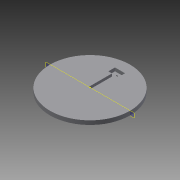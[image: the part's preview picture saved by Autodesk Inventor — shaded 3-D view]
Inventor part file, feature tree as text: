
AUTODESK INVENTOR PART (.ipt)
format: ipt  version: 2015 SP1 (Build 190203100, 203)  size: 104,960 bytes
history: native  units: mm
features: sketch x5, extrude x4, other x1, projected_geometry x1
ambient origin geometry x8: Origin, YZ Plane, XZ Plane, XY Plane, X Axis, Y Axis, Z Axis, Center Point
bodies: Body1 (feature_tree)
feature tree (11):
  other  "Sólido1"
  extrude  "Extrusión1"  Depth=6.0mm TaperAngle=0.0deg
  sketch  "Boceto2"  dims[d3=15.0mm d4=10.0mm]
  extrude  "Extrusión2"  Depth=10.0mm
  extrude  "Extrusión3"  Depth=5.0mm
  extrude  "Extrusión4"  Depth=10.0mm TaperAngle=0.0deg
  sketch  "Boceto1"  dims[d0=120.0mm d1=6.0mm d2=0.0mm]
  sketch  "Boceto3"  dims[d5=5.0mm d6=0.0mm d7=3.0mm]
  sketch  "Boceto4"  dims[d8=5.0mm d9=0.0mm d12=10.0mm d13=0.0mm]
  sketch  "Boceto5"  dims[d14=35.0mm d15=2.0mm d16=2.0mm d17=3.0mm]
  projected_geometry  "Contorno proyectado1"
